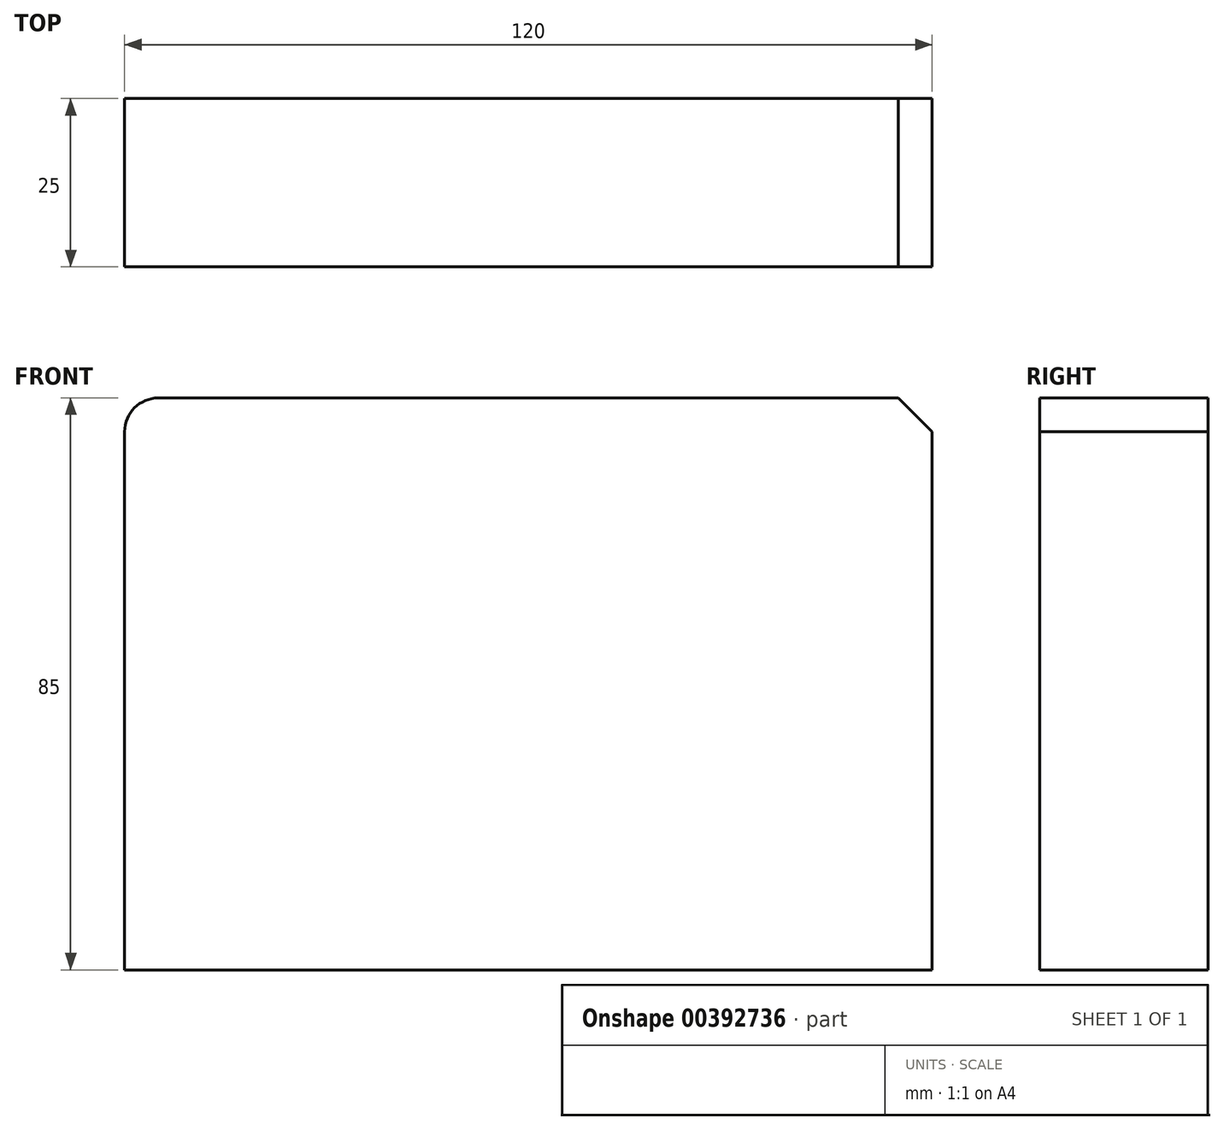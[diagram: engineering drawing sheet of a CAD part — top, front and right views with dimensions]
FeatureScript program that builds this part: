
annotation { "Feature Type Name" : "Feature", "Feature Type Description" : "" }
export const myFeature = defineFeature(function(context is Context, id is Id, definition is map)
    precondition{}
    {
        {
            var Q0;
            Q0=qCreatedBy(makeId("Front.planeOp"),FACE);
            var sketch = newSketch(context, id + "F0", { "sketchPlane" : qUnion([Q0])});
            skLineSegment(sketch, "E0.bottom", {"start": v(60, -42.5) * mm, "end": v(-60, -42.5) * mm});
            skLineSegment(sketch, "E0.top", {"start": v(60, 42.5) * mm, "end": v(-60, 42.5) * mm});
            skLineSegment(sketch, "E0.left", {"start": v(60, -42.5) * mm, "end": v(60, 42.5) * mm});
            skLineSegment(sketch, "E0.right", {"start": v(-60, -42.5) * mm, "end": v(-60, 42.5) * mm});
            skPoint(sketch, "E0.middle", {"position": v(0, 0) * mm});
            skSolve(sketch);
        }
        {
            var Q0;
            Q0 = qSketchRegion(id + "F0", true);
            var Q1;
            Q1=makeQuery(id+"F0.imprint","IMPRINT",FACE,{"disambiguationData":[TD([[makeQuery(id+"F0.imprint","IMPRINT",EDGE,{"derivedFrom":sQuery(id+"F0.wireOp",EDGE,"E0.bottom")}),-1.0]])]});
            extrude(context, id + "F1", {"entities" : qUnion([Q0, Q1]), "endBound" : BoundingType.SYMMETRIC, "depth" : 25 * mm});
        }
        {
            var Q0;
            Q0=makeQuery(id+"F1.opExtrude","SWEPT_EDGE",EDGE,{"disambiguationData":[OSD([sQuery(id+"F0.wireOp",EDGE,"E0.top"),sQuery(id+"F0.wireOp",EDGE,"E0.right")])]});
            fillet(context, id + "F2", {"entities" : qUnion([Q0]), "radius" : 5 * mm, "tangentPropagation" : true, "allowEdgeOverflow" : false});
        }
        {
            var Q0;
            Q0=makeQuery(id+"F1.opExtrude","SWEPT_EDGE",EDGE,{"disambiguationData":[OSD([sQuery(id+"F0.wireOp",EDGE,"E0.top"),sQuery(id+"F0.wireOp",EDGE,"E0.left")])]});
            chamfer(context, id + "F3", {"entities" : qUnion([Q0]), "width" : 5 * mm, "tangentPropagation" : true});
        }
    });
